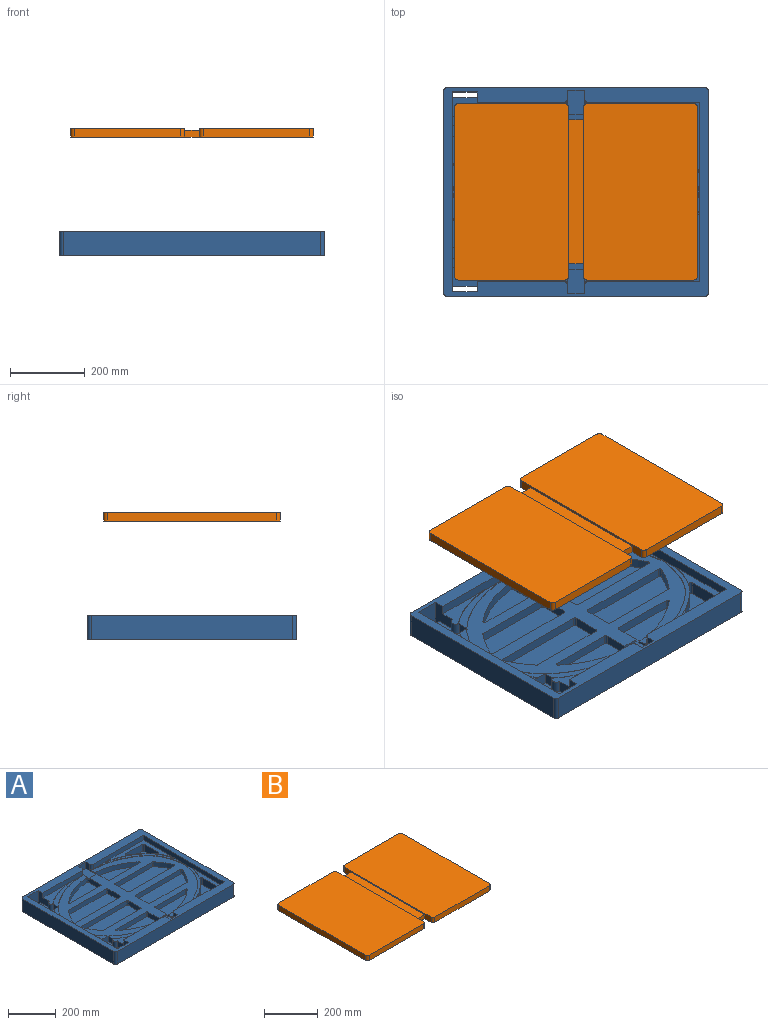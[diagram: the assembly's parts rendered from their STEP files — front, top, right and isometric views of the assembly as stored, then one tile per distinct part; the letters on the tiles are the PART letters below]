
ASSEMBLY  parts=2 mates=1
PART A: 167 faces, bbox 710x560x65 mm
  f0: plane 105x65mm, normal (0,0,1), area 6334.1mm2, adj f1,f2,f54,f55,f56,f81,f84
  f1: plane 30x29mm, normal (-1,0,0), area 868mm2, adj f0,f4,f6,f14,f55,f84
  f2: plane 536x65mm, normal (1,0,0), area 19326.7mm2, adj f0,f3,f7,f9,f18,f20,f53,f55
  f3: plane 149.61x65.59mm, normal (0,0,1), area 1975.8mm2, adj f2,f5,f7,f55
  f4: plane 244.65x92.57mm, normal (0,0,1), area 3510.4mm2, adj f1,f6,f8,f11,f76,f83
  f5: extruded ~148x63.98mm, area 329.2mm2, adj f3,f14,f55,f89
  f6: extruded ~243.09x91.01mm, area 531.2mm2, adj f1,f4,f14,f76,f77
  f7: extruded ~79.84x35.3mm, area 175.2mm2, adj f2,f3,f9,f55
  f8: extruded ~158.45x59.76mm, area 343.6mm2, adj f4,f10,f11,f83
  f9: plane 80.67x36.14mm, normal (0,0,1), area 1234.7mm2, adj f2,f7,f55
  f10: plane 170.95x62mm, normal (0,0,1), area 3568.8mm2, adj f8,f11,f54,f83,f84
  f11: plane 232.5x26mm, normal (0,1,0), area 5728.1mm2, adj f4,f8,f10,f18,f54,f64
  f12: plane 297.5x26mm, normal (0,1,0), area 7269.4mm2, adj f13,f15,f18,f65,f78,f80
  f13: plane 308.09x240mm, normal (0,0,1), area 3828.1mm2, adj f12,f15,f66,f67,f70,f78,f79
  f14: plane 660x480mm, normal (0,0,1), area 118962.5mm2, adj f1,f5,f6,f19,f24,f25,f26,f27
  f15: plane 480x26mm, normal (-1,0,0), area 11722.7mm2, adj f12,f13,f18,f79,f80,f96,f97,f157
  f16: plane 10x10mm, normal (0,0,1), area 21.5mm2, adj f61,f65,f66
  f17: plane 10x10mm, normal (0,0,1), area 21.5mm2, adj f59,f64,f76
  f18: plane 710x560mm, normal (0,0,1), area 74108.3mm2, adj f2,f11,f12,f15,f21,f22,f23,f53
  f19: cylinder r=5mm len=25mm, axis (0,0,1), area 193.3mm2, adj f14,f24,f28,f29,f59,f62
  f20: plane 710x560mm, normal (0,0,-1), area 395564.2mm2, adj f2,f21,f22,f23,f53,f54,f56,f57
  f21: plane 540x65mm, normal (-1,0,0), area 35100mm2, adj f18,f20,f57,f135
  f22: plane 690x65mm, normal (0,-1,0), area 44850mm2, adj f18,f20,f57,f58
  f23: plane 540x65mm, normal (1,0,0), area 35100mm2, adj f18,f20,f58,f136
  f24: plane 73.59x25mm, normal (-1,0,0), area 1800.3mm2, adj f14,f19,f25,f29,f60,f62
  f25: cylinder r=5mm len=25mm, axis (0,0,1), area 196.3mm2, adj f14,f24,f26,f29
  f26: plane 179.25x25mm, normal (0,-1,0), area 4481.3mm2, adj f14,f25,f27,f29
  f27: cylinder r=5mm len=25mm, axis (0,0,1), area 305.8mm2, adj f14,f26,f28,f29
  f28: cylinder r=327mm len=182.04mm, axis (0,0,1), area 4996.9mm2, adj f14,f19,f27,f29
  f29: plane 189.25x83.59mm, normal (0,0,1), area 10859.5mm2, adj f19,f24,f25,f26,f27,f28
  f30: cylinder r=5mm len=25mm, axis (0,0,1), area 196.3mm2, adj f14,f31,f36,f37
  f31: plane 267.47x25mm, normal (0,-1,0), area 6686.7mm2, adj f14,f30,f32,f37
  f32: cylinder r=5mm len=25mm, axis (0,0,1), area 248.4mm2, adj f14,f31,f33,f37
  f33: cylinder r=327mm len=76.16mm, axis (0,0,1), area 2245.9mm2, adj f14,f32,f34,f37
  f34: cylinder r=5mm len=25mm, axis (0,0,1), area 109.9mm2, adj f14,f33,f35,f37
  f35: plane 221.09x25mm, normal (0,1,0), area 5527.1mm2, adj f14,f34,f37,f166
  f36: plane 75x25mm, normal (-1,0,0), area 1875mm2, adj f14,f30,f37,f166
  f37: plane 277.47x85mm, normal (0,0,1), area 21837.9mm2, adj f30,f31,f32,f33,f34,f35,f36,f166
  f38: cylinder r=5mm len=25mm, axis (0,0,1), area 248.4mm2, adj f14,f39,f44,f45
  f39: plane 267.47x25mm, normal (0,-1,0), area 6686.7mm2, adj f14,f38,f40,f45
  f40: cylinder r=5mm len=25mm, axis (0,0,1), area 196.3mm2, adj f14,f39,f41,f45
  f41: plane 75x25mm, normal (1,0,0), area 1875mm2, adj f14,f40,f45,f165
  f42: plane 221.09x25mm, normal (0,1,0), area 5527.1mm2, adj f14,f43,f45,f165
  f43: cylinder r=5mm len=25mm, axis (0,0,1), area 109.9mm2, adj f14,f42,f44,f45
  f44: cylinder r=327mm len=76.16mm, axis (0,0,1), area 2245.9mm2, adj f14,f38,f43,f45
  f45: plane 277.47x85mm, normal (0,0,1), area 21837.9mm2, adj f38,f39,f40,f41,f42,f43,f44,f165
  f46: cylinder r=5mm len=25mm, axis (0,0,1), area 196.3mm2, adj f14,f47,f51,f52
  f47: plane 73.59x25mm, normal (1,0,0), area 1800.3mm2, adj f14,f46,f48,f52,f60,f62
  f48: cylinder r=5mm len=25mm, axis (0,0,1), area 193.3mm2, adj f14,f47,f49,f52,f61,f62
  f49: cylinder r=327mm len=182.04mm, axis (0,0,1), area 4996.9mm2, adj f14,f48,f50,f52
  f50: cylinder r=5mm len=25mm, axis (0,0,1), area 305.8mm2, adj f14,f49,f51,f52
  f51: plane 179.25x25mm, normal (0,-1,0), area 4481.3mm2, adj f14,f46,f50,f52
  f52: plane 189.25x83.59mm, normal (0,0,1), area 10859.5mm2, adj f46,f47,f48,f49,f50,f51
  f53: plane 65x65mm, normal (0,1,0), area 4225mm2, adj f2,f18,f20,f54
  f54: plane 65x65mm, normal (-1,0,0), area 2837mm2, adj f0,f10,f11,f18,f20,f53,f56,f84
  f55: plane 65x31mm, normal (0,-1,0), area 1953.6mm2, adj f0,f1,f2,f3,f5,f7,f9,f14
  f56: plane 65x10mm, normal (0,-1,0), area 650mm2, adj f0,f2,f20,f54
  f57: cylinder r=10mm len=65mm, axis (0,0,-1), area 1021mm2, adj f18,f20,f21,f22
  f58: cylinder r=10mm len=65mm, axis (0,0,-1), area 1021mm2, adj f18,f20,f22,f23
  f59: plane 56.23x34mm, normal (1,0,0), area 953.4mm2, adj f14,f17,f18,f19,f62,f63,f64,f77
  f60: plane 44x6mm, normal (0,-1,0), area 264mm2, adj f14,f24,f47,f62
  f61: plane 56.23x34mm, normal (-1,0,0), area 953.4mm2, adj f14,f16,f18,f48,f62,f63,f65,f68
  f62: plane 65x45mm, normal (0,0,1), area 2916.9mm2, adj f19,f24,f47,f48,f59,f60,f61,f63
  f63: plane 45x34mm, normal (0,1,0), area 1530mm2, adj f18,f59,f61,f62
  f64: cylinder r=10mm len=28mm, axis (0,0,-1), area 439.8mm2, adj f11,f17,f18,f59,f76
  f65: cylinder r=10mm len=28mm, axis (0,0,1), area 439.8mm2, adj f12,f16,f18,f61,f66
  f66: plane 10.59x2mm, normal (0,-1,0), area 21.2mm2, adj f13,f16,f65,f67,f68
  f67: extruded ~308.09x240mm, area 863.2mm2, adj f13,f14,f66,f68,f145
  f68: plane 0.59x0mm, normal (0,0,-1), area 0mm2, adj f61,f66,f67
  f69: plane 109.62x94.71mm, normal (0,0,1), area 5342.2mm2, adj f70,f71,f72,f73,f74,f75
  f70: cylinder r=347mm len=98.2mm, axis (0,0,1), area 4575.2mm2, adj f13,f69,f71,f75,f78,f79,f80
  f71: cylinder r=5mm len=36mm, axis (0,0,1), area 472.3mm2, adj f69,f70,f72,f80
  f72: plane 99.62x36mm, normal (0,1,0), area 3586.3mm2, adj f69,f71,f73,f80
  f73: cylinder r=5mm len=36mm, axis (0,0,1), area 282.7mm2, adj f69,f72,f74,f80
  f74: plane 84.71x36mm, normal (-1,0,0), area 3049.5mm2, adj f69,f73,f75,f80
  f75: cylinder r=5mm len=36mm, axis (0,0,1), area 443.2mm2, adj f69,f70,f74,f80
  f76: plane 10.59x2mm, normal (0,-1,0), area 21.2mm2, adj f4,f6,f17,f64,f77
  f77: plane 0.59x0mm, normal (0,0,-1), area 0mm2, adj f6,f59,f76
  f78: extruded ~164.44x71.49mm, area 363.4mm2, adj f12,f13,f70,f80
  f79: extruded ~84.89x35.91mm, area 185.5mm2, adj f13,f15,f70,f80
  f80: plane 232.78x189.32mm, normal (0,0,1), area 6853.1mm2, adj f12,f15,f70,f71,f72,f73,f74,f75
  f81: cylinder r=12.5mm len=31mm, axis (0,0,-1), area 1217.4mm2, adj f0,f2,f82
  f82: plane 25x12.5mm, normal (0,0,1), area 245.4mm2, adj f2,f81
  f83: plane 2.24x2mm, normal (1,0,0), area 4.5mm2, adj f4,f8,f10,f84
  f84: cylinder r=12.5mm len=31mm, axis (0,0,-1), area 1217.4mm2, adj f0,f1,f10,f54,f83
  f85: plane 105x65mm, normal (0,0,1), area 6334.1mm2, adj f2,f86,f132,f133,f134,f159,f162
  f86: plane 30x29mm, normal (-1,0,0), area 868mm2, adj f14,f85,f88,f90,f133,f162
  f87: plane 149.61x65.59mm, normal (0,0,1), area 1975.8mm2, adj f2,f89,f91,f133
  f88: plane 244.65x92.57mm, normal (0,0,1), area 3510.4mm2, adj f86,f90,f92,f95,f154,f161
  f89: extruded ~148x63.98mm, area 329.2mm2, adj f5,f14,f87,f133
  f90: extruded ~243.09x91.01mm, area 531.2mm2, adj f14,f86,f88,f154,f155
  f91: extruded ~79.84x35.3mm, area 175.2mm2, adj f2,f87,f93,f133
  f92: extruded ~158.45x59.76mm, area 343.6mm2, adj f88,f94,f95,f161
  f93: plane 80.67x36.14mm, normal (0,0,1), area 1234.7mm2, adj f2,f91,f133
  f94: plane 170.95x62mm, normal (0,0,1), area 3568.8mm2, adj f92,f95,f132,f161,f162
  f95: plane 232.5x26mm, normal (0,-1,0), area 5728.1mm2, adj f18,f88,f92,f94,f132,f142
  f96: plane 297.5x26mm, normal (0,-1,0), area 7269.4mm2, adj f15,f18,f97,f143,f156,f158
  f97: plane 308.09x240mm, normal (0,0,1), area 3828.1mm2, adj f15,f96,f144,f145,f148,f156,f157
  f98: plane 10x10mm, normal (0,0,1), area 21.5mm2, adj f139,f143,f144
  f99: plane 10x10mm, normal (0,0,1), area 21.5mm2, adj f137,f142,f154
  f100: cylinder r=5mm len=25mm, axis (0,0,1), area 193.3mm2, adj f14,f102,f106,f107,f137,f140
  f101: plane 690x65mm, normal (0,1,0), area 44850mm2, adj f18,f20,f135,f136
  f102: plane 73.59x25mm, normal (-1,0,0), area 1800.3mm2, adj f14,f100,f103,f107,f138,f140
  f103: cylinder r=5mm len=25mm, axis (0,0,1), area 196.3mm2, adj f14,f102,f104,f107
  f104: plane 179.25x25mm, normal (0,1,0), area 4481.3mm2, adj f14,f103,f105,f107
  f105: cylinder r=5mm len=25mm, axis (0,0,1), area 305.8mm2, adj f14,f104,f106,f107
  f106: cylinder r=327mm len=182.04mm, axis (0,0,1), area 4996.9mm2, adj f14,f100,f105,f107
  f107: plane 189.25x83.59mm, normal (0,0,1), area 10859.5mm2, adj f100,f102,f103,f104,f105,f106
  f108: cylinder r=5mm len=25mm, axis (0,0,1), area 196.3mm2, adj f14,f109,f114,f115
  f109: plane 267.47x25mm, normal (0,1,0), area 6686.7mm2, adj f14,f108,f110,f115
  f110: cylinder r=5mm len=25mm, axis (0,0,1), area 248.4mm2, adj f14,f109,f111,f115
  f111: cylinder r=327mm len=76.16mm, axis (0,0,1), area 2245.9mm2, adj f14,f110,f112,f115
  f112: cylinder r=5mm len=25mm, axis (0,0,1), area 109.9mm2, adj f14,f111,f113,f115
  f113: plane 221.09x25mm, normal (0,-1,0), area 5527.1mm2, adj f14,f112,f115,f163
  f114: plane 75x25mm, normal (-1,0,0), area 1875mm2, adj f14,f108,f115,f163
  f115: plane 277.47x85mm, normal (0,0,1), area 21837.9mm2, adj f108,f109,f110,f111,f112,f113,f114,f163
  f116: cylinder r=5mm len=25mm, axis (0,0,1), area 248.4mm2, adj f14,f117,f122,f123
  f117: plane 267.47x25mm, normal (0,1,0), area 6686.7mm2, adj f14,f116,f118,f123
  f118: cylinder r=5mm len=25mm, axis (0,0,1), area 196.3mm2, adj f14,f117,f119,f123
  f119: plane 75x25mm, normal (1,0,0), area 1875mm2, adj f14,f118,f123,f164
  f120: plane 221.09x25mm, normal (0,-1,0), area 5527.1mm2, adj f14,f121,f123,f164
  f121: cylinder r=5mm len=25mm, axis (0,0,1), area 109.9mm2, adj f14,f120,f122,f123
  f122: cylinder r=327mm len=76.16mm, axis (0,0,1), area 2245.9mm2, adj f14,f116,f121,f123
  f123: plane 277.47x85mm, normal (0,0,1), area 21837.9mm2, adj f116,f117,f118,f119,f120,f121,f122,f164
  f124: cylinder r=5mm len=25mm, axis (0,0,1), area 196.3mm2, adj f14,f125,f129,f130
  f125: plane 73.59x25mm, normal (1,0,0), area 1800.3mm2, adj f14,f124,f126,f130,f138,f140
  f126: cylinder r=5mm len=25mm, axis (0,0,1), area 193.3mm2, adj f14,f125,f127,f130,f139,f140
  f127: cylinder r=327mm len=182.04mm, axis (0,0,1), area 4996.9mm2, adj f14,f126,f128,f130
  f128: cylinder r=5mm len=25mm, axis (0,0,1), area 305.8mm2, adj f14,f127,f129,f130
  f129: plane 179.25x25mm, normal (0,1,0), area 4481.3mm2, adj f14,f124,f128,f130
  f130: plane 189.25x83.59mm, normal (0,0,1), area 10859.5mm2, adj f124,f125,f126,f127,f128,f129
  f131: plane 65x65mm, normal (0,-1,0), area 4225mm2, adj f2,f18,f20,f132
  f132: plane 65x65mm, normal (-1,0,0), area 2837mm2, adj f18,f20,f85,f94,f95,f131,f134,f162
  f133: plane 65x31mm, normal (0,1,0), area 1953.6mm2, adj f2,f14,f85,f86,f87,f89,f91,f93
  f134: plane 65x10mm, normal (0,1,0), area 650mm2, adj f2,f20,f85,f132
  f135: cylinder r=10mm len=65mm, axis (0,0,-1), area 1021mm2, adj f18,f20,f21,f101
  f136: cylinder r=10mm len=65mm, axis (0,0,-1), area 1021mm2, adj f18,f20,f23,f101
  f137: plane 56.23x34mm, normal (1,0,0), area 953.4mm2, adj f14,f18,f99,f100,f140,f141,f142,f155
  f138: plane 44x6mm, normal (0,1,0), area 264mm2, adj f14,f102,f125,f140
  f139: plane 56.23x34mm, normal (-1,0,0), area 953.4mm2, adj f14,f18,f98,f126,f140,f141,f143,f146
  f140: plane 65x45mm, normal (0,0,1), area 2916.9mm2, adj f100,f102,f125,f126,f137,f138,f139,f141
  f141: plane 45x34mm, normal (0,-1,0), area 1530mm2, adj f18,f137,f139,f140
  f142: cylinder r=10mm len=28mm, axis (0,0,-1), area 439.8mm2, adj f18,f95,f99,f137,f154
  f143: cylinder r=10mm len=28mm, axis (0,0,1), area 439.8mm2, adj f18,f96,f98,f139,f144
  f144: plane 10.59x2mm, normal (0,1,0), area 21.2mm2, adj f97,f98,f143,f145,f146
  f145: extruded ~308.09x240mm, area 863.2mm2, adj f14,f67,f97,f144,f146
  f146: plane 0.59x0mm, normal (0,0,-1), area 0mm2, adj f139,f144,f145
  f147: plane 109.62x94.71mm, normal (0,0,1), area 5342.2mm2, adj f148,f149,f150,f151,f152,f153
  f148: cylinder r=347mm len=98.2mm, axis (0,0,1), area 4575.2mm2, adj f97,f147,f149,f153,f156,f157,f158
  f149: cylinder r=5mm len=36mm, axis (0,0,1), area 472.3mm2, adj f147,f148,f150,f158
  f150: plane 99.62x36mm, normal (0,-1,0), area 3586.3mm2, adj f147,f149,f151,f158
  f151: cylinder r=5mm len=36mm, axis (0,0,1), area 282.7mm2, adj f147,f150,f152,f158
  f152: plane 84.71x36mm, normal (-1,0,0), area 3049.5mm2, adj f147,f151,f153,f158
  f153: cylinder r=5mm len=36mm, axis (0,0,1), area 443.2mm2, adj f147,f148,f152,f158
  f154: plane 10.59x2mm, normal (0,1,0), area 21.2mm2, adj f88,f90,f99,f142,f155
  f155: plane 0.59x0mm, normal (0,0,-1), area 0mm2, adj f90,f137,f154
  f156: extruded ~164.44x71.49mm, area 363.4mm2, adj f96,f97,f148,f158
  f157: extruded ~84.89x35.91mm, area 185.5mm2, adj f15,f97,f148,f158
  f158: plane 232.78x189.32mm, normal (0,0,1), area 6853.1mm2, adj f15,f96,f148,f149,f150,f151,f152,f153
  f159: cylinder r=12.5mm len=31mm, axis (0,0,-1), area 1217.4mm2, adj f2,f85,f160
  f160: plane 25x12.5mm, normal (0,0,1), area 245.4mm2, adj f2,f159
  f161: plane 2.24x2mm, normal (1,0,0), area 4.5mm2, adj f88,f92,f94,f162
  f162: cylinder r=12.5mm len=31mm, axis (0,0,-1), area 1217.4mm2, adj f85,f86,f94,f132,f161
  f163: cylinder r=5mm len=25mm, axis (0,0,-1), area 196.3mm2, adj f14,f113,f114,f115
  f164: cylinder r=5mm len=25mm, axis (0,0,-1), area 196.3mm2, adj f14,f119,f120,f123
  f165: cylinder r=5mm len=25mm, axis (0,0,-1), area 196.3mm2, adj f14,f41,f42,f45
  f166: cylinder r=5mm len=25mm, axis (0,0,-1), area 196.3mm2, adj f14,f35,f36,f37
PART B: 22 faces, bbox 650x473x24 mm
  f0: plane 453x24mm, normal (-1,0,0), area 10872mm2, adj f4,f5,f18,f21
  f1: plane 285x24mm, normal (0,-1,0), area 6840mm2, adj f4,f5,f18,f19
  f2: plane 453x24mm, normal (1,0,0), area 3942mm2, adj f4,f5,f6,f7,f8,f19,f20
  f3: plane 285x24mm, normal (0,1,0), area 6840mm2, adj f4,f5,f20,f21
  f4: plane 473x305mm, normal (0,0,1), area 144179.2mm2, adj f0,f1,f2,f3,f18,f19,f20,f21
  f5: plane 650x473mm, normal (0,0,-1), area 303758.3mm2, adj f0,f1,f2,f3,f6,f7,f9,f10
  f6: plane 40x18mm, normal (0,-1,0), area 720mm2, adj f2,f5,f8,f11
  f7: plane 40x18mm, normal (0,1,0), area 720mm2, adj f2,f5,f8,f11
  f8: plane 385x40mm, normal (0,0,1), area 15400mm2, adj f2,f6,f7,f11
  f9: plane 453x24mm, normal (1,0,0), area 10872mm2, adj f5,f13,f16,f17
  f10: plane 285x24mm, normal (0,-1,0), area 6840mm2, adj f5,f13,f14,f17
  f11: plane 453x24mm, normal (-1,0,0), area 3942mm2, adj f5,f6,f7,f8,f13,f14,f15
  f12: plane 285x24mm, normal (0,1,0), area 6840mm2, adj f5,f13,f15,f16
  f13: plane 473x305mm, normal (0,0,1), area 144179.2mm2, adj f9,f10,f11,f12,f14,f15,f16,f17
  f14: cylinder r=10mm len=24mm, axis (0,0,-1), area 377mm2, adj f5,f10,f11,f13
  f15: cylinder r=10mm len=24mm, axis (0,0,-1), area 377mm2, adj f5,f11,f12,f13
  f16: cylinder r=10mm len=24mm, axis (0,0,-1), area 377mm2, adj f5,f9,f12,f13
  f17: cylinder r=10mm len=24mm, axis (0,0,-1), area 377mm2, adj f5,f9,f10,f13
  f18: cylinder r=10mm len=24mm, axis (0,0,-1), area 377mm2, adj f0,f1,f4,f5
  f19: cylinder r=10mm len=24mm, axis (0,0,-1), area 377mm2, adj f1,f2,f4,f5
  f20: cylinder r=10mm len=24mm, axis (0,0,-1), area 377mm2, adj f2,f3,f4,f5
  f21: cylinder r=10mm len=24mm, axis (0,0,-1), area 377mm2, adj f0,f3,f4,f5
PLACE A t=(-700.87,-279.81,-0.46)mm
PLACE B t=(-670.87,-516.31,318.21)mm
MATE slider B.f5 <-> A.f14  axis (0,0,-1) through (-345.87,-279.81,318.21)mm
